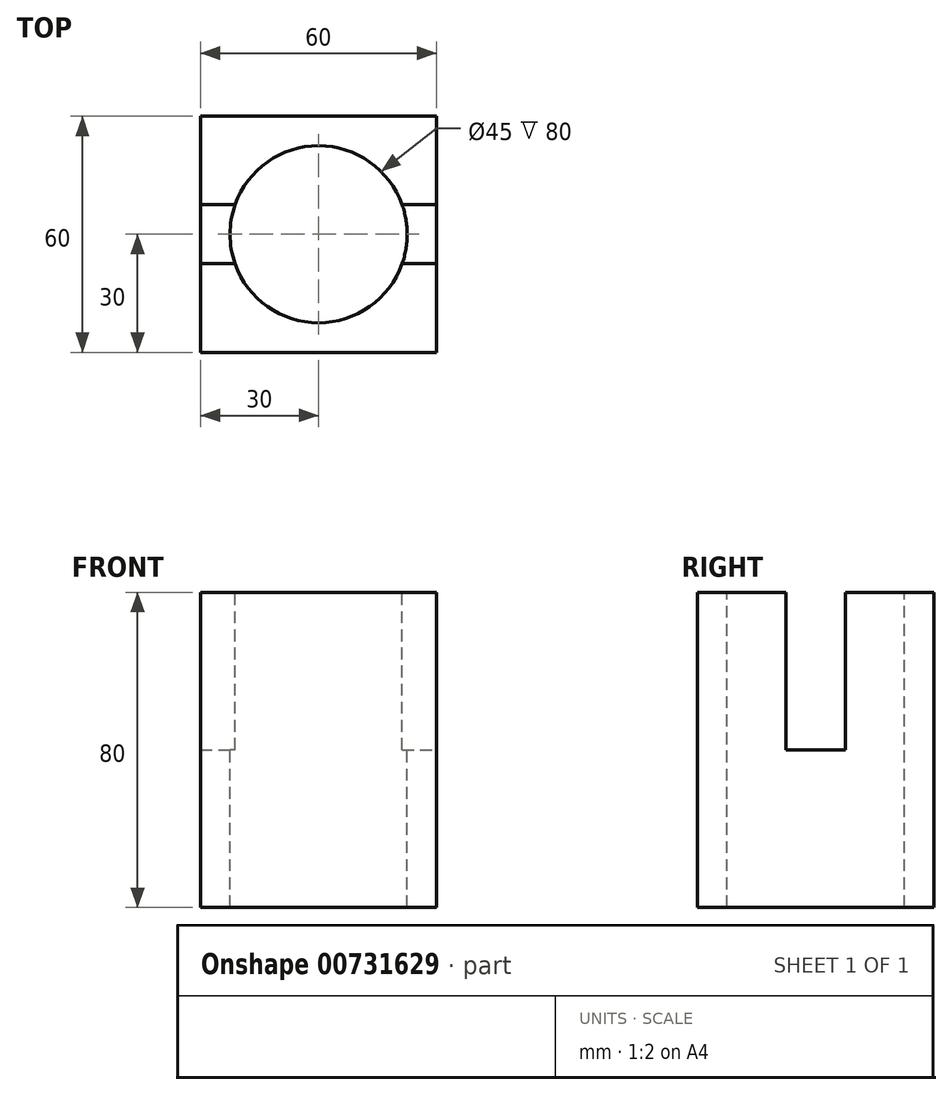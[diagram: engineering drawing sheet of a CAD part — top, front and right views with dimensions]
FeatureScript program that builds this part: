
annotation { "Feature Type Name" : "Feature", "Feature Type Description" : "" }
export const myFeature = defineFeature(function(context is Context, id is Id, definition is map)
    precondition{}
    {
        {
            var Q0;
            Q0=qCreatedBy(makeId("Top.planeOp"),FACE);
            var sketch = newSketch(context, id + "F0", { "sketchPlane" : qUnion([Q0])});
            skLineSegment(sketch, "E0.bottom", {"start": v(-30, 30) * mm, "end": v(30, 30) * mm});
            skLineSegment(sketch, "E0.top", {"start": v(-30, -30) * mm, "end": v(30, -30) * mm});
            skLineSegment(sketch, "E0.left", {"start": v(-30, 30) * mm, "end": v(-30, -30) * mm});
            skLineSegment(sketch, "E0.right", {"start": v(30, 30) * mm, "end": v(30, -30) * mm});
            skSolve(sketch);
        }
        {
            var Q0;
            Q0=makeQuery(id+"F0.imprint","IMPRINT",FACE,{"disambiguationData":[TD([[makeQuery(id+"F0.imprint","IMPRINT",EDGE,{"derivedFrom":sQuery(id+"F0.wireOp",EDGE,"E0.bottom")}),-1.0]])]});
            extrude(context, id + "F1", {"entities" : qUnion([Q0]), "depth" : 80 * mm, "offsetDistance" : 25 * mm});
        }
        {
            var Q0;
            Q0=makeQuery(id+"F1.opExtrude","CAP_FACE",FACE,{"disambiguationData":[OSD([sQuery(id+"F0.wireOp",EDGE,"E0.bottom"),sQuery(id+"F0.wireOp",EDGE,"E0.top"),sQuery(id+"F0.wireOp",EDGE,"E0.left"),sQuery(id+"F0.wireOp",EDGE,"E0.right")])],"isStart":false});
            var sketch = newSketch(context, id + "F2", { "sketchPlane" : qUnion([Q0])});
            skCircle(sketch, "E1", {"center": v(0, 0) * mm, "radius": 22.5 * mm});
            skSolve(sketch);
        }
        {
            var Q0;
            Q0=makeQuery(id+"F2.imprint","IMPRINT",FACE,{"disambiguationData":[TD([[makeQuery(id+"F2.imprint","IMPRINT",EDGE,{"derivedFrom":sQuery(id+"F2.wireOp",EDGE,"E1")}),1.0]])]});
            extrude(context, id + "F3", {"entities" : qUnion([Q0]), "operationType" : NewBodyOperationType.REMOVE, "oppositeDirection" : true, "depth" : 80 * mm, "offsetDistance" : 25 * mm});
        }
        {
            var Q0;
            Q0=makeQuery(id+"F1.opExtrude","SWEPT_FACE",FACE,{"disambiguationData":[OSD([sQuery(id+"F0.wireOp",EDGE,"E0.right")])]});
            var sketch = newSketch(context, id + "F4", { "sketchPlane" : qUnion([Q0])});
            skLineSegment(sketch, "E2.bottom", {"start": v(7.5, 40) * mm, "end": v(-7.5, 40) * mm});
            skLineSegment(sketch, "E2.top", {"start": v(7.5, 80) * mm, "end": v(-7.5, 80) * mm});
            skLineSegment(sketch, "E2.left", {"start": v(7.5, 40) * mm, "end": v(7.5, 80) * mm});
            skLineSegment(sketch, "E2.right", {"start": v(-7.5, 40) * mm, "end": v(-7.5, 80) * mm});
            skSolve(sketch);
        }
        {
            var Q0;
            Q0=makeQuery(id+"F4.imprint","IMPRINT",FACE,{"disambiguationData":[TD([[makeQuery(id+"F4.imprint","IMPRINT",EDGE,{"derivedFrom":sQuery(id+"F4.wireOp",EDGE,"E2.bottom")}),-1.0]])]});
            extrude(context, id + "F5", {"entities" : qUnion([Q0]), "operationType" : NewBodyOperationType.REMOVE, "oppositeDirection" : true, "depth" : 60 * mm, "offsetDistance" : 25 * mm});
        }
    });
